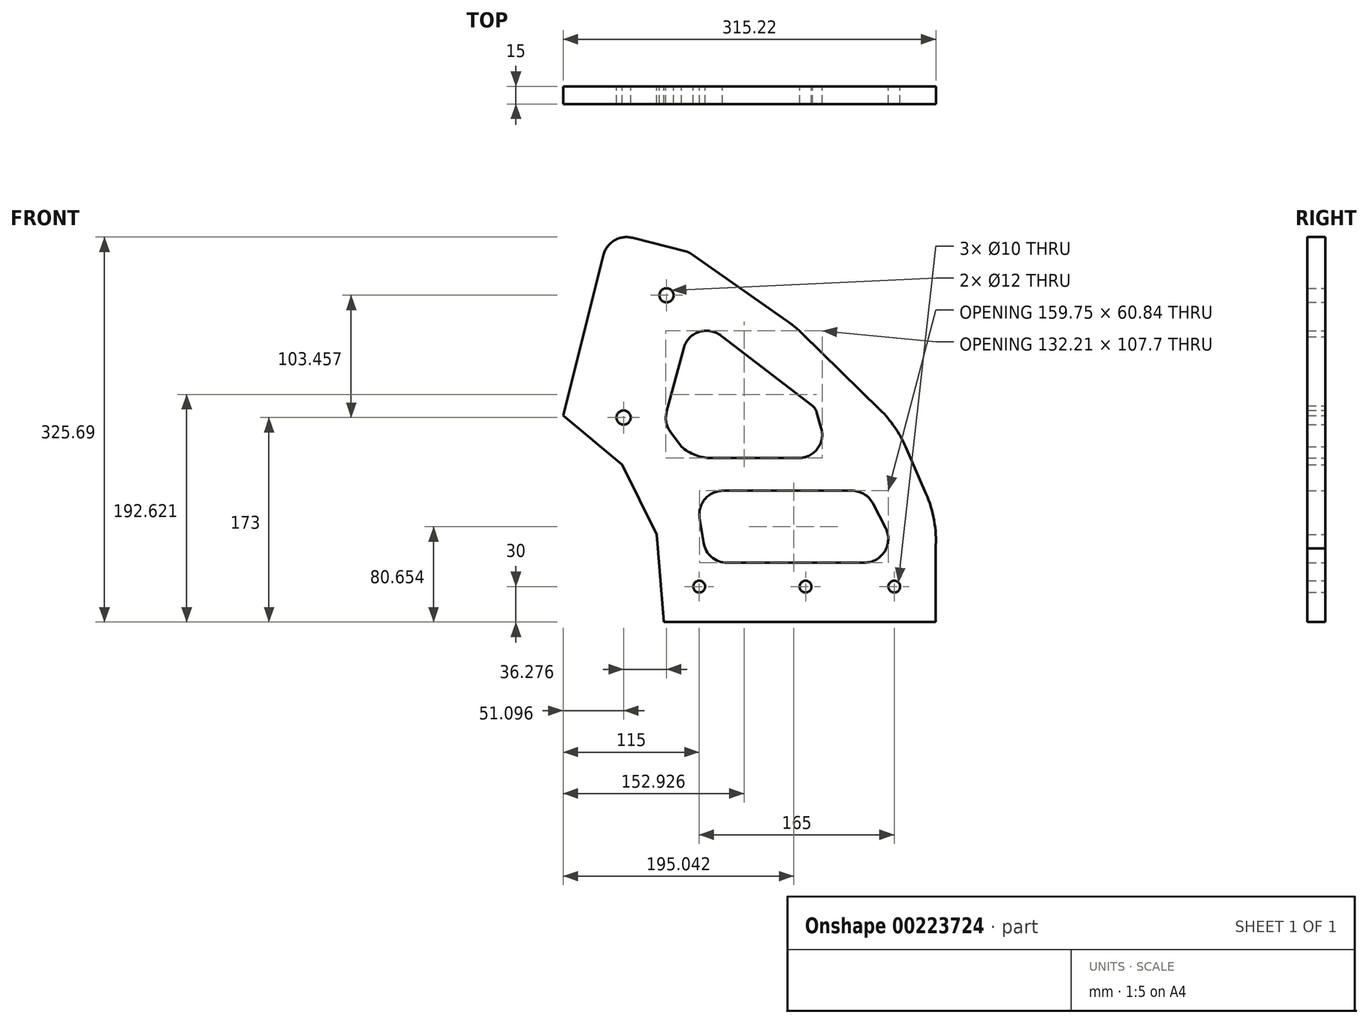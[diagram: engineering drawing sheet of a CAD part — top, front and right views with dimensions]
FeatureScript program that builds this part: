
annotation { "Feature Type Name" : "Feature", "Feature Type Description" : "" }
export const myFeature = defineFeature(function(context is Context, id is Id, definition is map)
    precondition{}
    {
        {
            var Q0;
            Q0=qCreatedBy(makeId("Front.planeOp"),FACE);
            var sketch = newSketch(context, id + "F0", { "sketchPlane" : qUnion([Q0])});
            skLineSegment(sketch, "E0", {"start": v(0, 0) * mm, "end": v(230, 0) * mm});
            skLineSegment(sketch, "E1", {"start": v(-85, 174.81) * mm, "end": v(-50.93, 310.55) * mm});
            skLineSegment(sketch, "E2", {"start": v(-6, 74) * mm, "end": v(-35, 133) * mm});
            skLineSegment(sketch, "E3", {"start": v(-35, 133) * mm, "end": v(-85, 174.81) * mm});
            skCircle(sketch, "E4", {"center": v(-33.9, 173) * mm, "radius": 6 * mm});
            skCircle(sketch, "E5", {"center": v(2.37, 276.46) * mm, "radius": 6 * mm});
            skLineSegment(sketch, "E6", {"start": v(-26.62, 325.07) * mm, "end": v(19.41, 313.4) * mm});
            skLineSegment(sketch, "E7", {"start": v(53.44, 50.24) * mm, "end": v(169.93, 50.24) * mm});
            skLineSegment(sketch, "E8", {"start": v(30.38, 87.94) * mm, "end": v(32.2, 76.48) * mm});
            skLineSegment(sketch, "E9", {"start": v(32.2, 76.48) * mm, "end": v(33.7, 67.1) * mm});
            skPoint(sketch, "E10.visualSharp", {"position": v(36.37, 50.24) * mm});
            skArc(sketch, "E10.filletArc", {"start": v(33.7, 67.1) * mm, "mid": v(40.46, 55.02) * mm, "end": v(53.44, 50.24) * mm});
            skPoint(sketch, "E11.visualSharp", {"position": v(26.7, 111.07) * mm});
            skArc(sketch, "E11.filletArc", {"start": v(50.13, 111.07) * mm, "mid": v(34.92, 104.06) * mm, "end": v(30.38, 87.94) * mm});
            skPoint(sketch, "E12.visualSharp", {"position": v(35.66, 54.68) * mm});
            skLineSegment(sketch, "E12.filletArc", {"start": v(32.2, 76.48) * mm, "end": v(32.2, 76.48) * mm});
            skPoint(sketch, "E13.visualSharp", {"position": v(-46.05, 330) * mm});
            skArc(sketch, "E13.filletArc", {"start": v(-26.62, 325.07) * mm, "mid": v(-41.79, 322.86) * mm, "end": v(-50.93, 310.55) * mm});
            skLineSegment(sketch, "E14", {"start": v(0, 0) * mm, "end": v(-6, 74) * mm});
            skCircle(sketch, "E15", {"center": v(30, 30) * mm, "radius": 5 * mm});
            skCircle(sketch, "E16", {"center": v(120, 30) * mm, "radius": 5 * mm});
            skCircle(sketch, "E17", {"center": v(195, 30) * mm, "radius": 5 * mm});
            skLineSegment(sketch, "E18", {"start": v(187.7, 79.41) * mm, "end": v(176.93, 100.25) * mm});
            skPoint(sketch, "E19.visualSharp", {"position": v(202.77, 50.24) * mm});
            skArc(sketch, "E19.filletArc", {"start": v(169.93, 50.24) * mm, "mid": v(187.01, 59.83) * mm, "end": v(187.7, 79.41) * mm});
            skLineSegment(sketch, "E20", {"start": v(221.86, 108.75) * mm, "end": v(204.64, 148.2) * mm});
            skLineSegment(sketch, "E21", {"start": v(183, 179.6) * mm, "end": v(117.1, 244.2) * mm});
            skLineSegment(sketch, "E22", {"start": v(104.37, 254.75) * mm, "end": v(22.34, 312.06) * mm});
            skPoint(sketch, "E23.visualSharp", {"position": v(21, 313) * mm});
            skArc(sketch, "E23.filletArc", {"start": v(22.34, 312.06) * mm, "mid": v(20.94, 312.87) * mm, "end": v(19.41, 313.4) * mm});
            skPoint(sketch, "E24.visualSharp", {"position": v(111.17, 250) * mm});
            skArc(sketch, "E24.filletArc", {"start": v(117.1, 244.2) * mm, "mid": v(110.95, 249.74) * mm, "end": v(104.37, 254.75) * mm});
            skPoint(sketch, "E25.visualSharp", {"position": v(196.87, 166) * mm});
            skArc(sketch, "E25.filletArc", {"start": v(204.64, 148.2) * mm, "mid": v(195.33, 164.94) * mm, "end": v(183, 179.6) * mm});
            skPoint(sketch, "E26.visualSharp", {"position": v(234.42, 80) * mm});
            skArc(sketch, "E26.filletArc", {"start": v(230, 62.18) * mm, "mid": v(228.72, 85.95) * mm, "end": v(221.86, 108.75) * mm});
            skLineSegment(sketch, "E27", {"start": v(40.23, 138.77) * mm, "end": v(114.27, 138.77) * mm});
            skLineSegment(sketch, "E28", {"start": v(133.3, 164) * mm, "end": v(129.49, 177.31) * mm});
            skPoint(sketch, "E29.visualSharp", {"position": v(128.54, 180.64) * mm});
            skArc(sketch, "E29.filletArc", {"start": v(129.49, 177.31) * mm, "mid": v(128.12, 180.37) * mm, "end": v(125.95, 182.93) * mm});
            skPoint(sketch, "E30.visualSharp", {"position": v(140.5, 138.77) * mm});
            skArc(sketch, "E30.filletArc", {"start": v(114.27, 138.77) * mm, "mid": v(130.06, 146.64) * mm, "end": v(133.3, 164) * mm});
            skPoint(sketch, "E31.visualSharp", {"position": v(18.84, 138.77) * mm});
            skArc(sketch, "E31.filletArc", {"start": v(14.9, 148.38) * mm, "mid": v(26.69, 141.25) * mm, "end": v(40.23, 138.77) * mm});
            skLineSegment(sketch, "E32", {"start": v(50.13, 111.07) * mm, "end": v(159.16, 111.07) * mm});
            skPoint(sketch, "E33.visualSharp", {"position": v(171.34, 111.07) * mm});
            skArc(sketch, "E33.filletArc", {"start": v(176.93, 100.25) * mm, "mid": v(169.57, 108.16) * mm, "end": v(159.16, 111.07) * mm});
            skLineSegment(sketch, "E34", {"start": v(230, 62.18) * mm, "end": v(230, 0) * mm});
            skLineSegment(sketch, "E35", {"start": v(-85, 174.81) * mm, "end": v(-85, 398.37) * mm, "construction": true});
            skLineSegment(sketch, "E36", {"start": v(14.9, 148.38) * mm, "end": v(5.73, 160.77) * mm});
            skLineSegment(sketch, "E37", {"start": v(2.48, 177.82) * mm, "end": v(16.83, 231.63) * mm});
            skPoint(sketch, "E38.visualSharp", {"position": v(28.45, 275.22) * mm});
            skArc(sketch, "E38.filletArc", {"start": v(49.67, 241.22) * mm, "mid": v(30.55, 245.68) * mm, "end": v(16.83, 231.63) * mm});
            skPoint(sketch, "E39.visualSharp", {"position": v(0, 168.51) * mm});
            skArc(sketch, "E39.filletArc", {"start": v(2.48, 177.82) * mm, "mid": v(2.16, 168.93) * mm, "end": v(5.73, 160.77) * mm});
            skLineSegment(sketch, "E40", {"start": v(125.95, 182.93) * mm, "end": v(49.67, 241.22) * mm});
            skLineSegment(sketch, "E41", {"start": v(-93.7, 175) * mm, "end": v(-62.14, 175) * mm, "construction": true});
            skSolve(sketch);
        }
        {
            var Q0;
            Q0=qSketchRegion(id+"F0",true);
            var Q1;
            Q1=makeQuery(id+"F0.imprint","IMPRINT",FACE,{"disambiguationData":[TD([[makeQuery(id+"F0.imprint","IMPRINT",EDGE,{"derivedFrom":sQuery(id+"F0.wireOp",EDGE,"E0")}),1.0]])]});
            extrude(context, id + "F1", {"entities" : qUnion([Q0, Q1]), "depth" : 15 * mm});
        }
    });
